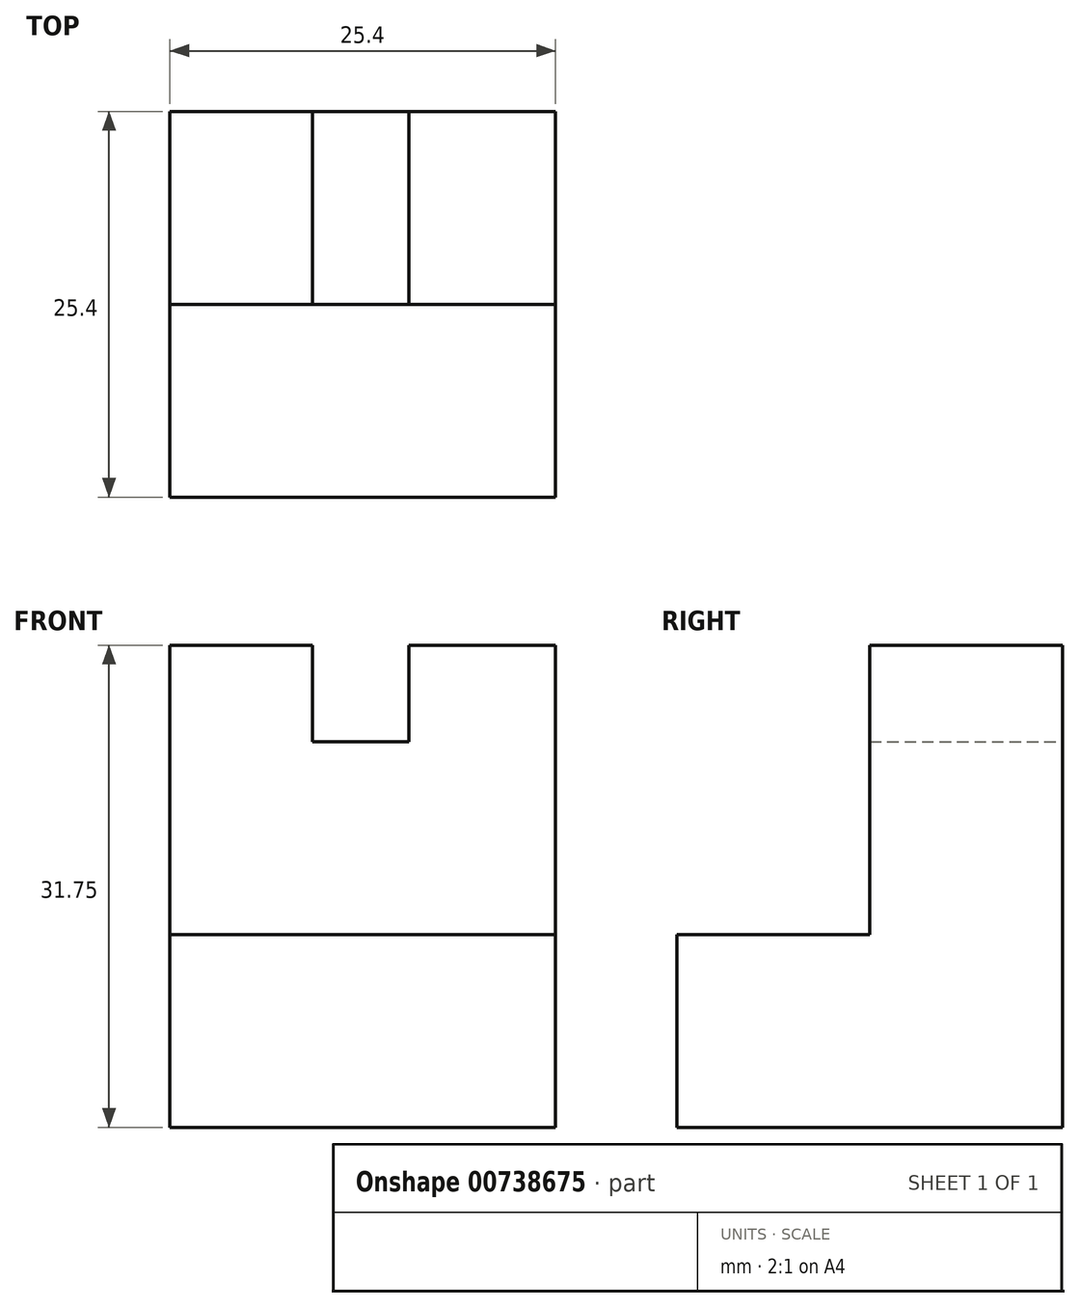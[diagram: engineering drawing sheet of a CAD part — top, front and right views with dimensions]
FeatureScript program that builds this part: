
annotation { "Feature Type Name" : "Feature", "Feature Type Description" : "" }
export const myFeature = defineFeature(function(context is Context, id is Id, definition is map)
    precondition{}
    {
        {
            var Q0;
            Q0=qCreatedBy(makeId("Right.planeOp"),FACE);
            var sketch = newSketch(context, id + "F0", { "sketchPlane" : qUnion([Q0])});
            skLineSegment(sketch, "E0", {"start": v(0, 0) * mm, "end": v(-25.4, 0) * mm});
            skLineSegment(sketch, "E1", {"start": v(-25.4, 0) * mm, "end": v(-25.4, 12.7) * mm});
            skLineSegment(sketch, "E2", {"start": v(-25.4, 12.7) * mm, "end": v(-12.7, 12.7) * mm});
            skLineSegment(sketch, "E3", {"start": v(-12.7, 12.7) * mm, "end": v(-12.7, 31.75) * mm});
            skLineSegment(sketch, "E4", {"start": v(-12.7, 31.75) * mm, "end": v(0, 31.75) * mm});
            skLineSegment(sketch, "E5", {"start": v(0, 31.75) * mm, "end": v(0, 0) * mm});
            skSolve(sketch);
        }
        {
            var Q0;
            Q0 = qSketchRegion(id + "F0", true);
            extrude(context, id + "F1", {"entities" : qUnion([Q0]), "depth" : 25.4 * mm, "offsetDistance" : 25.4 * mm});
        }
        {
            var Q0;
            Q0=makeQuery(id+"F1.opExtrude","SWEPT_FACE",FACE,{"disambiguationData":[OSD([sQuery(id+"F0.wireOp",EDGE,"E5")])]});
            var sketch = newSketch(context, id + "F2", { "sketchPlane" : qUnion([Q0])});
            skLineSegment(sketch, "E6", {"start": v(-15.75, 31.75) * mm, "end": v(-15.75, 25.4) * mm});
            skLineSegment(sketch, "E7", {"start": v(-15.75, 25.4) * mm, "end": v(-9.4, 25.4) * mm});
            skLineSegment(sketch, "E8", {"start": v(-9.4, 25.4) * mm, "end": v(-9.4, 31.75) * mm});
            skLineSegment(sketch, "E9", {"start": v(-15.75, 31.75) * mm, "end": v(-9.4, 31.75) * mm});
            skSolve(sketch);
        }
        {
            var Q0;
            Q0=makeQuery(id+"F2.imprint","IMPRINT",FACE,{"disambiguationData":[TD([[makeQuery(id+"F2.imprint","IMPRINT",EDGE,{"derivedFrom":sQuery(id+"F2.wireOp",EDGE,"E6")}),1.0]])]});
            extrude(context, id + "F3", {"entities" : qUnion([Q0]), "operationType" : NewBodyOperationType.REMOVE, "endBound" : BoundingType.THROUGH_ALL, "oppositeDirection" : true, "depth" : 25.4 * mm, "offsetDistance" : 25.4 * mm});
        }
    });
